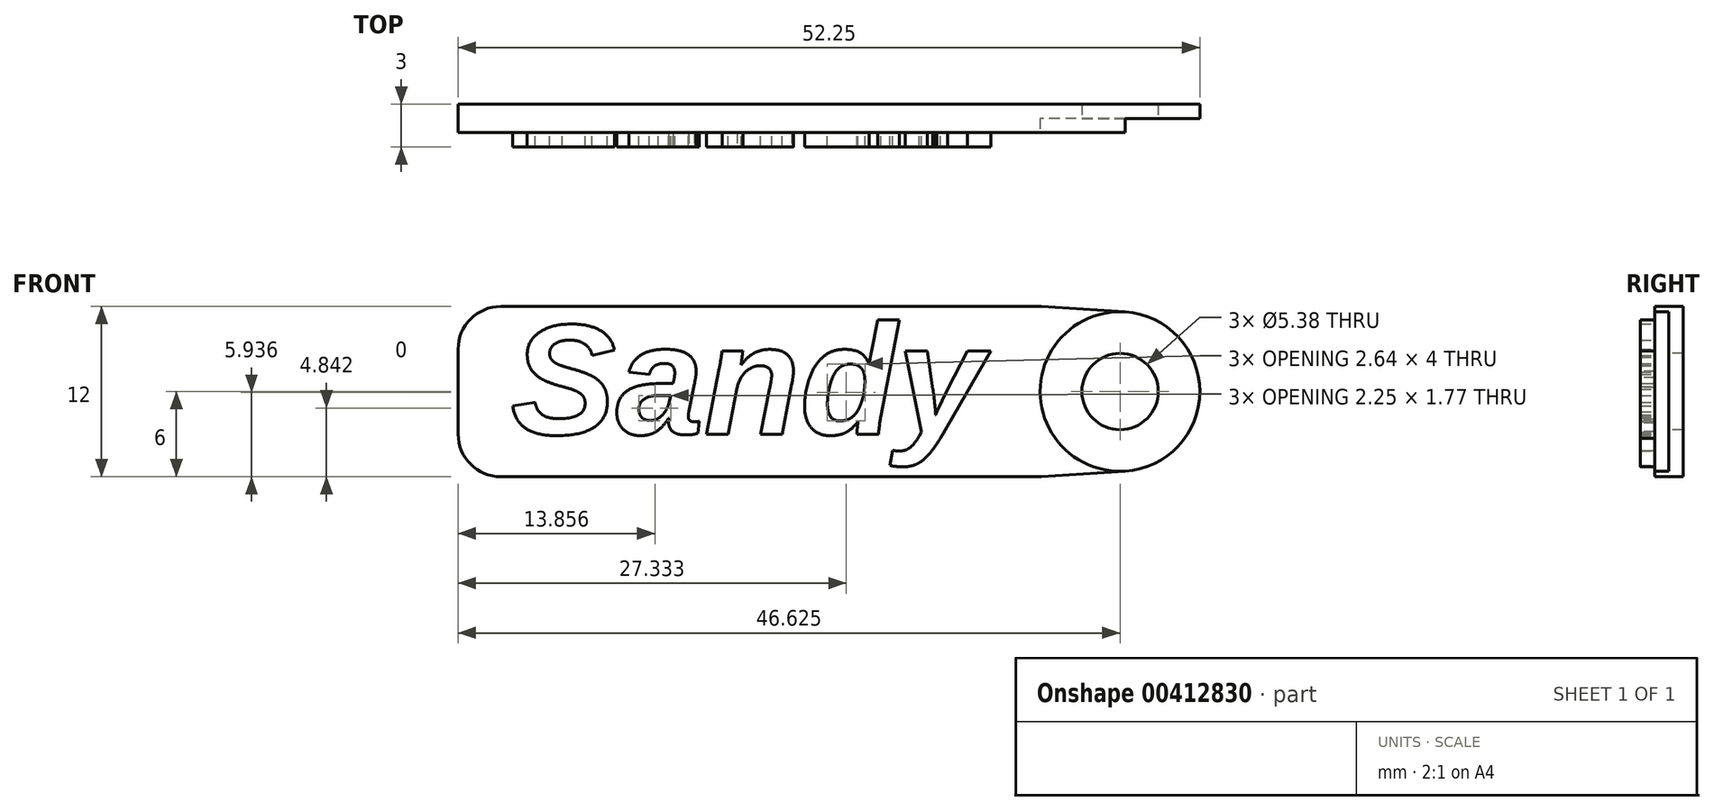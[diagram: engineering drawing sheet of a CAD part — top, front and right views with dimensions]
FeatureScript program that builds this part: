
annotation { "Feature Type Name" : "Feature", "Feature Type Description" : "" }
export const myFeature = defineFeature(function(context is Context, id is Id, definition is map)
    precondition{}
    {
        {
            var Q0;
            Q0=qCreatedBy(makeId("Front.planeOp"),FACE);
            var sketch = newSketch(context, id + "F0", { "sketchPlane" : qUnion([Q0])});
            skText(sketch, "E0", { "text": "Sandy", "fontName": "Arimo-BoldItalic.ttf"});
            const initialGuessF0  = {"E0": [-0.01729, -0.008, 1, 0, 0.008]};
            skSetInitialGuess(sketch, initialGuessF0);
            skSolve(sketch);
        }
        {
            var Q0;
            Q0=qSketchRegion(id+"F0",true);
            extrude(context, id + "F1", {"entities" : qUnion([Q0]), "depth" : 1 * mm});
        }
        {
            var Q0;
            Q0=qCreatedBy(makeId("Front.planeOp"),FACE);
            var sketch = newSketch(context, id + "F2", { "sketchPlane" : qUnion([Q0])});
            skLineSegment(sketch, "E1", {"start": v(20, -11) * mm, "end": v(-21, -11) * mm});
            skLineSegment(sketch, "E2", {"start": v(-21, 1) * mm, "end": v(20, 1) * mm});
            skLineSegment(sketch, "E3", {"start": v(20, -11) * mm, "end": v(20, 1) * mm, "construction": true});
            skLineSegment(sketch, "E4", {"start": v(-21, -11) * mm, "end": v(-21, 1) * mm});
            skCircle(sketch, "E5", {"center": v(25.63, -5) * mm, "radius": 5.62 * mm});
            skLineSegment(sketch, "E6", {"start": v(20, -5) * mm, "end": v(67.35, -5) * mm, "construction": true});
            skPoint(sketch, "E6.endSnap0", {"position": v(20, -5) * mm});
            skLineSegment(sketch, "E7", {"start": v(20, 1) * mm, "end": v(25.99, 0.61) * mm});
            skLineSegment(sketch, "E8", {"start": v(25.99, -10.61) * mm, "end": v(20, -11) * mm});
            skCircle(sketch, "E9", {"center": v(25.63, -5) * mm, "radius": 2.69 * mm});
            skSolve(sketch);
        }
        {
            var Q0;
            Q0=qSketchRegion(id+"F2",true);
            extrude(context, id + "F3", {"entities" : qUnion([Q0]), "oppositeDirection" : true, "depth" : 2 * mm});
        }
        {
            var Q0;
            Q0=makeQuery(id+"F3.opExtrude","SWEPT_EDGE",EDGE,{"disambiguationData":[OSD([sQuery(id+"F2.wireOp",EDGE,"E2"),sQuery(id+"F2.wireOp",EDGE,"E4")])]});
            var Q1;
            Q1=makeQuery(id+"F3.opExtrude","SWEPT_EDGE",EDGE,{"disambiguationData":[OSD([sQuery(id+"F2.wireOp",EDGE,"E1"),sQuery(id+"F2.wireOp",EDGE,"E4")])]});
            var Q2;
            Q2=makeQuery(id+"F3.opExtrude","SWEPT_EDGE",EDGE,{"disambiguationData":[OSD([sQuery(id+"F2.wireOp",EDGE,"E1"),sQuery(id+"F2.wireOp",EDGE,"E8")])]});
            var Q3;
            Q3=makeQuery(id+"F3.opExtrude","SWEPT_EDGE",EDGE,{"disambiguationData":[OSD([sQuery(id+"F2.wireOp",EDGE,"E2"),sQuery(id+"F2.wireOp",EDGE,"E7")])]});
            fillet(context, id + "F4", {"entities" : qUnion([Q0, Q1, Q2, Q3]), "radius" : 3 * mm, "tangentPropagation" : true, "allowEdgeOverflow" : false});
        }
        {
            var Q0;
            Q0=makeQuery(id+"F3.opExtrude","CAP_FACE",FACE,{"disambiguationData":[OSD([sQuery(id+"F2.wireOp",EDGE,"E1"),sQuery(id+"F2.wireOp",EDGE,"E2"),sQuery(id+"F2.wireOp",EDGE,"E4"),sQuery(id+"F2.wireOp",EDGE,"E5"),sQuery(id+"F2.wireOp",EDGE,"E7"),sQuery(id+"F2.wireOp",EDGE,"E8"),sQuery(id+"F2.wireOp",EDGE,"E9")])],"isStart":true});
            var sketch = newSketch(context, id + "F5", { "sketchPlane" : qUnion([Q0])});
            skCircle(sketch, "E10", {"center": v(25.63, -5) * mm, "radius": 5.62 * mm});
            skSolve(sketch);
        }
        {
            var Q0;
            Q0=qSketchRegion(id+"F5",true);
            extrude(context, id + "F6", {"entities" : qUnion([Q0]), "operationType" : NewBodyOperationType.REMOVE, "oppositeDirection" : true, "depth" : 1 * mm});
        }
    });
